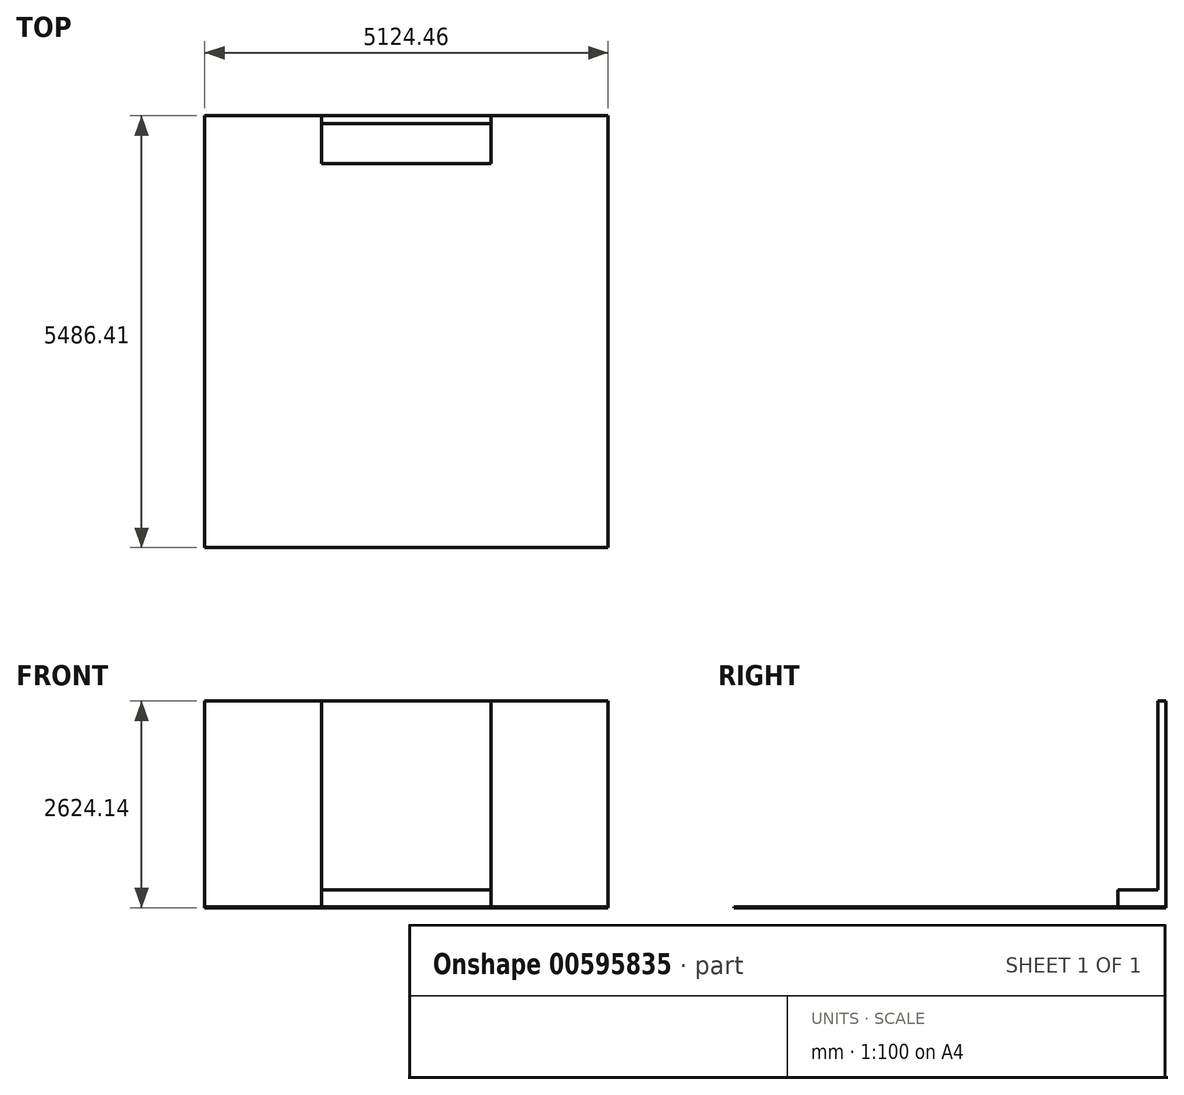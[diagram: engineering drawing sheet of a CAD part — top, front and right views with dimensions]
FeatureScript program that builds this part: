
annotation { "Feature Type Name" : "Feature", "Feature Type Description" : "" }
export const myFeature = defineFeature(function(context is Context, id is Id, definition is map)
    precondition{}
    {
        {
            var Q0;
            Q0=qCreatedBy(makeId("Front.planeOp"),FACE);
            var sketch = newSketch(context, id + "F0", { "sketchPlane" : qUnion([Q0])});
            skLineSegment(sketch, "E0.bottom", {"start": v(-2562.23, -7.94) * mm, "end": v(2562.23, -7.94) * mm});
            skLineSegment(sketch, "E0.top", {"start": v(-2562.23, 0) * mm, "end": v(2562.23, 0) * mm});
            skLineSegment(sketch, "E0.left", {"start": v(-2562.23, -7.94) * mm, "end": v(-2562.23, 0) * mm});
            skLineSegment(sketch, "E0.right", {"start": v(2562.23, -7.94) * mm, "end": v(2562.23, 0) * mm});
            skLineSegment(sketch, "E1.bottom", {"start": v(-1076.33, 0) * mm, "end": v(1076.33, 0) * mm});
            skLineSegment(sketch, "E1.top", {"start": v(-1076.33, 215.9) * mm, "end": v(1076.33, 215.9) * mm});
            skLineSegment(sketch, "E1.left", {"start": v(-1076.33, 0) * mm, "end": v(-1076.33, 215.9) * mm});
            skLineSegment(sketch, "E1.right", {"start": v(1076.33, 0) * mm, "end": v(1076.33, 215.9) * mm});
            skLineSegment(sketch, "E2", {"start": v(0, 215.9) * mm, "end": v(0, 0) * mm});
            skLineSegment(sketch, "E3.top", {"start": v(-1076.33, 2616.2) * mm, "end": v(1076.32, 2616.2) * mm});
            skLineSegment(sketch, "E3.left", {"start": v(-1076.33, 215.9) * mm, "end": v(-1076.33, 2616.2) * mm});
            skLineSegment(sketch, "E3.right", {"start": v(1076.33, 215.9) * mm, "end": v(1076.33, 2616.2) * mm});
            skSolve(sketch);
        }
        {
            var Q0;
            Q0=makeQuery(id+"F0.imprint","IMPRINT",FACE,{"disambiguationData":[TD([[makeQuery(id+"F0.imprint","IMPRINT",EDGE,{"derivedFrom":sQuery(id+"F0.wireOp",EDGE,"E0.bottom")}),1.0]])]});
            extrude(context, id + "F1", {"entities" : qUnion([Q0]), "depth" : 5486.4 * mm, "offsetDistance" : 25.4 * mm});
        }
        {
            var Q0;
            {var subQ0=sQuery(id+"F0.wireOp",EDGE,"E1.right");Q0=makeQuery(id+"F0.imprint","IMPRINT",FACE,{"disambiguationData":[TD([[makeQuery(id+"F0.imprint","IMPRINT",EDGE,{"derivedFrom":subQ0}),1.0]])]});}
            var Q1;
            {var subQ0=sQuery(id+"F0.wireOp",EDGE,"E1.left");Q1=makeQuery(id+"F0.imprint","IMPRINT",FACE,{"disambiguationData":[TD([[makeQuery(id+"F0.imprint","IMPRINT",EDGE,{"derivedFrom":subQ0}),-1.0]])]});}
            extrude(context, id + "F2", {"entities" : qUnion([Q0, Q1]), "depth" : 609.6 * mm, "offsetDistance" : 25.4 * mm});
        }
        {
            var Q0;
            Q0=makeQuery(id+"F0.imprint","IMPRINT",FACE,{"disambiguationData":[TD([[makeQuery(id+"F0.imprint","IMPRINT",EDGE,{"derivedFrom":sQuery(id+"F0.wireOp",EDGE,"E3.top")}),-1.0]])]});
            extrude(context, id + "F3", {"entities" : qUnion([Q0]), "operationType" : NewBodyOperationType.ADD, "depth" : 101.6 * mm, "offsetDistance" : 25.4 * mm});
        }
        {
            var Q0;
            Q0=qCreatedBy(makeId("Front.planeOp"),FACE);
            var sketch = newSketch(context, id + "F4", { "sketchPlane" : qUnion([Q0])});
            skLineSegment(sketch, "E4.0", {"start": v(-2562.23, 0) * mm, "end": v(2562.23, 0) * mm});
            skLineSegment(sketch, "E5.0", {"start": v(-1076.33, 2616.2) * mm, "end": v(1076.32, 2616.2) * mm});
            skPoint(sketch, "E6.oppositeSnap0", {"position": v(0, 2616.2) * mm});
            skLineSegment(sketch, "E6.bottom", {"start": v(2562.23, 0) * mm, "end": v(-2562.23, 0) * mm});
            skLineSegment(sketch, "E6.top", {"start": v(2562.23, 2616.2) * mm, "end": v(-2562.23, 2616.2) * mm});
            skLineSegment(sketch, "E6.left", {"start": v(2562.23, 0) * mm, "end": v(2562.23, 2616.2) * mm});
            skLineSegment(sketch, "E6.right", {"start": v(-2562.23, 0) * mm, "end": v(-2562.23, 2616.2) * mm});
            skSolve(sketch);
        }
        {
            var Q0;
            Q0 = qSketchRegion(id + "F4", true);
            extrude(context, id + "F5", {"entities" : qUnion([Q0]), "oppositeDirection" : true, "depth" : 5 / 406.4 * mm, "offsetDistance" : 25.4 * mm});
        }
    });
